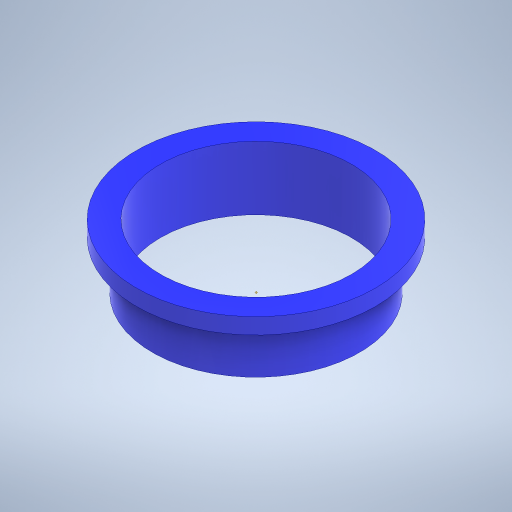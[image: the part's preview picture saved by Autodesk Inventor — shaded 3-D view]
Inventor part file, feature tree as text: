
AUTODESK INVENTOR PART (.ipt)
format: ipt  version: 2024 (Build 280153000, 153)  size: 263,680 bytes
history: native  units: mm
features: extrude x2, sketch x1
ambient origin geometry x8: Origin, YZ Plane, XZ Plane, XY Plane, X Axis, Y Axis, Z Axis, Center Point
bodies: Solid1 (feature_tree)
feature tree (3):
  extrude  "Extrusion1"  Depth=1.0mm
  extrude  "Extrusion2"  Depth=3.0mm TaperAngle=0.0deg
  sketch  "Sketch3"  dims[d0=12.0mm d1=13.0mm d2=3.0mm d3=0.0mm d4=15.0mm d5=1.0mm d6=0.0mm d7=12.0mm]
